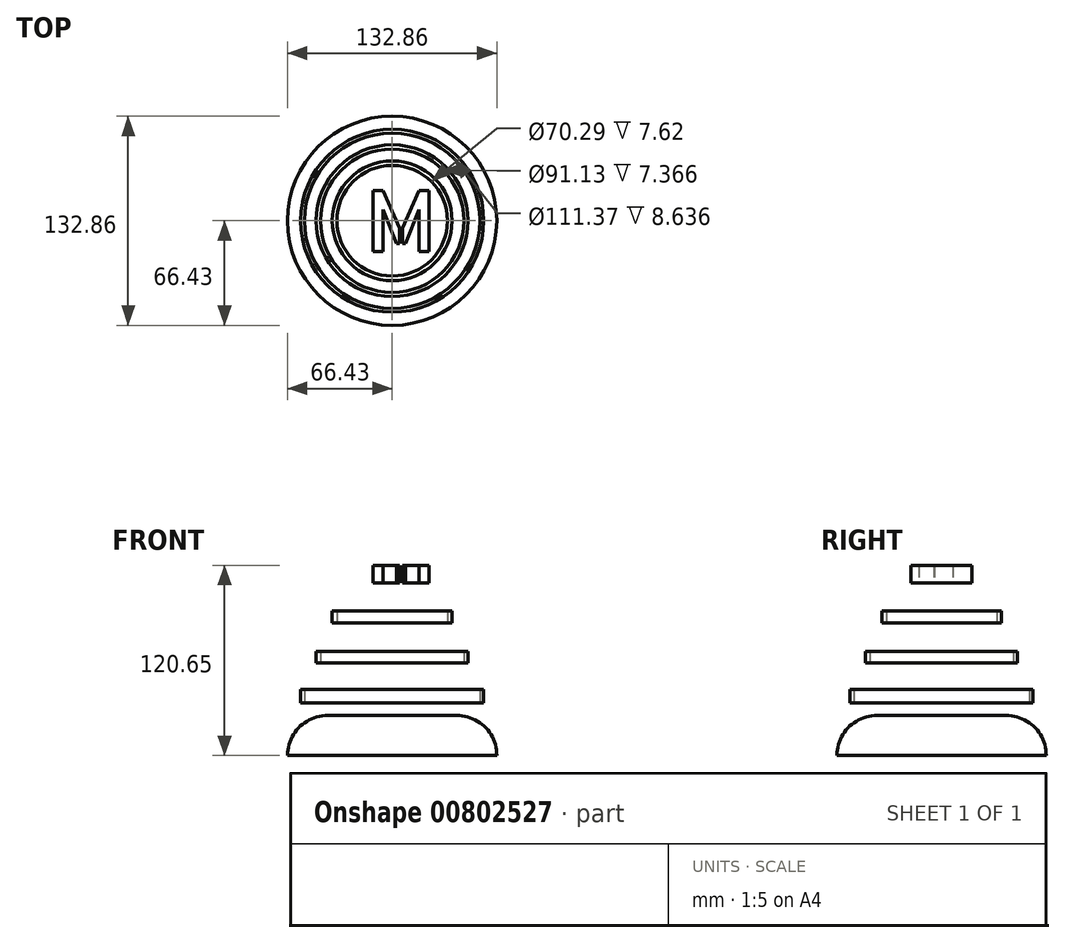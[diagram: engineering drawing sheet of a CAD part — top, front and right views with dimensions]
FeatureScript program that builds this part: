
annotation { "Feature Type Name" : "Feature", "Feature Type Description" : "" }
export const myFeature = defineFeature(function(context is Context, id is Id, definition is map)
    precondition{}
    {
        {
            var Q0;
            Q0=qCreatedBy(makeId("Top.planeOp"),FACE);
            var sketch = newSketch(context, id + "F0", { "sketchPlane" : qUnion([Q0])});
            skCircle(sketch, "E0", {"center": v(0, 0) * mm, "radius": 66.43 * mm});
            skSolve(sketch);
        }
        {
            var Q0;
            Q0 = qSketchRegion(id + "F0", true);
            extrude(context, id + "F1", {"entities" : qUnion([Q0]), "depth" : 25.4 * mm, "offsetDistance" : 25.4 * mm});
        }
        {
            var Q0;
            Q0=makeQuery(id+"F1.opExtrude","CAP_EDGE",EDGE,{"disambiguationData":[OSD([sQuery(id+"F0.wireOp",EDGE,"E0")])],"isStart":false});
            fillet(context, id + "F2", {"entities" : qUnion([Q0]), "radius" : 25.4 * mm, "tangentPropagation" : true, "allowEdgeOverflow" : false});
        }
        {
            var Q0;
            Q0=qCreatedBy(makeId("Top.planeOp"),FACE);
            cPlane(context, id + "F3", {"entities" : qUnion([Q0]), "cplaneType" : CPlaneType.OFFSET, "offset" : 33.27 * mm, "width" : 152.4 * mm, "height" : 152.4 * mm});
        }
        {
            var Q0;
            Q0=qCreatedBy(id+"F3.planeOp",FACE);
            cPlane(context, id + "F4", {"entities" : qUnion([Q0]), "cplaneType" : CPlaneType.OFFSET, "offset" : 25.4 * mm, "width" : 152.4 * mm, "height" : 152.4 * mm});
        }
        {
            var Q0;
            Q0=qCreatedBy(id+"F4.planeOp",FACE);
            cPlane(context, id + "F5", {"entities" : qUnion([Q0]), "cplaneType" : CPlaneType.OFFSET, "offset" : 25.4 * mm, "width" : 152.4 * mm, "height" : 152.4 * mm});
        }
        {
            var Q0;
            Q0=qCreatedBy(id+"F3.planeOp",FACE);
            var sketch = newSketch(context, id + "F6", { "sketchPlane" : qUnion([Q0])});
            skCircle(sketch, "E1", {"center": v(0, 0) * mm, "radius": 58.12 * mm});
            skCircle(sketch, "E2", {"center": v(0, 0) * mm, "radius": 55.69 * mm});
            skSolve(sketch);
        }
        {
            var Q0;
            Q0 = qSketchRegion(id + "F6", true);
            extrude(context, id + "F7", {"entities" : qUnion([Q0]), "depth" : 8.64 * mm, "offsetDistance" : 25.4 * mm});
        }
        {
            var Q0;
            Q0=qCreatedBy(id+"F4.planeOp",FACE);
            var sketch = newSketch(context, id + "F8", { "sketchPlane" : qUnion([Q0])});
            skCircle(sketch, "E3", {"center": v(0, 0) * mm, "radius": 48.23 * mm});
            skCircle(sketch, "E4", {"center": v(0, 0) * mm, "radius": 45.56 * mm});
            skSolve(sketch);
        }
        {
            var Q0;
            Q0 = qSketchRegion(id + "F8", true);
            extrude(context, id + "F9", {"entities" : qUnion([Q0]), "depth" : 7.37 * mm, "offsetDistance" : 25.4 * mm});
        }
        {
            var Q0;
            Q0=qCreatedBy(id+"F5.planeOp",FACE);
            var sketch = newSketch(context, id + "F10", { "sketchPlane" : qUnion([Q0])});
            skCircle(sketch, "E5", {"center": v(0, 0) * mm, "radius": 38.05 * mm});
            skCircle(sketch, "E6", {"center": v(0, 0) * mm, "radius": 35.15 * mm});
            skSolve(sketch);
        }
        {
            var Q0;
            Q0 = qSketchRegion(id + "F10", true);
            extrude(context, id + "F11", {"entities" : qUnion([Q0]), "depth" : 7.62 * mm, "offsetDistance" : 25.4 * mm});
        }
        {
            var Q0;
            Q0=qCreatedBy(id+"F5.planeOp",FACE);
            cPlane(context, id + "F12", {"entities" : qUnion([Q0]), "cplaneType" : CPlaneType.OFFSET, "offset" : 25.4 * mm, "width" : 152.4 * mm, "height" : 152.4 * mm});
        }
        {
            var Q0;
            Q0=qCreatedBy(id+"F12.planeOp",FACE);
            var sketch = newSketch(context, id + "F13", { "sketchPlane" : qUnion([Q0])});
            skText(sketch, "E7", { "text": "M", "fontName": "AllertaStencil-Regular.ttf"});
            const initialGuessF13  = {"E7": [-0.0171, -0.01951, 1, 0, 0.03876]};
            skSetInitialGuess(sketch, initialGuessF13);
            skSolve(sketch);
        }
        {
            var Q0;
            Q0 = qSketchRegion(id + "F13", true);
            extrude(context, id + "F14", {"entities" : qUnion([Q0]), "depth" : 11.18 * mm, "offsetDistance" : 25.4 * mm});
        }
    });
